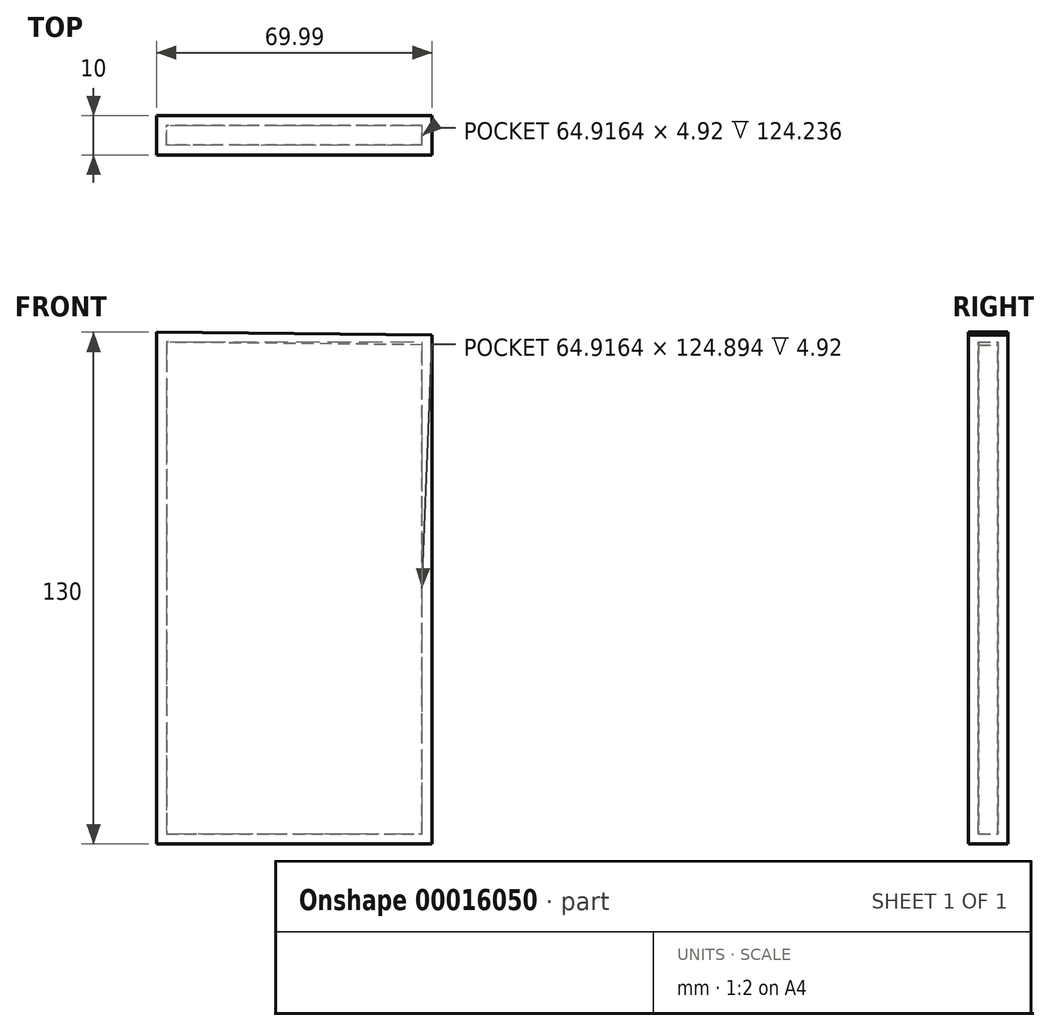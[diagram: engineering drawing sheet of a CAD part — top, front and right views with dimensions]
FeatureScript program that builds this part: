
annotation { "Feature Type Name" : "Feature", "Feature Type Description" : "" }
export const myFeature = defineFeature(function(context is Context, id is Id, definition is map)
    precondition{}
    {
        {
            var Q0;
            Q0=qCreatedBy(makeId("Front.planeOp"),FACE);
            var sketch = newSketch(context, id + "F0", { "sketchPlane" : qUnion([Q0])});
            skLineSegment(sketch, "E0", {"start": v(-56.41, 64.07) * mm, "end": v(-56.41, -65.93) * mm});
            skLineSegment(sketch, "E1", {"start": v(-56.41, -65.93) * mm, "end": v(13.58, -65.93) * mm});
            skLineSegment(sketch, "E2", {"start": v(13.58, -65.93) * mm, "end": v(13.58, 63.36) * mm});
            skLineSegment(sketch, "E3", {"start": v(13.58, 63.36) * mm, "end": v(-56.41, 64.07) * mm});
            skSolve(sketch);
        }
        {
            var Q0;
            Q0 = qSketchRegion(id + "F0", true);
            extrude(context, id + "F1", {"entities" : qUnion([Q0]), "depth" : 10 * mm});
        }
        {
            var Q0;
            Q0=makeQuery(id+"F1.opExtrude","CAP_FACE",FACE,{"disambiguationData":[OSD([sQuery(id+"F0.wireOp",EDGE,"E0"),sQuery(id+"F0.wireOp",EDGE,"E1"),sQuery(id+"F0.wireOp",EDGE,"E2"),sQuery(id+"F0.wireOp",EDGE,"E3")])],"isStart":true});
            var Q1;
            Q1=makeQuery(id+"F1.opExtrude","SWEPT_BODY",BODY,{"disambiguationData":[OSD([sQuery(id+"F0.wireOp",EDGE,"E0"),sQuery(id+"F0.wireOp",EDGE,"E1"),sQuery(id+"F0.wireOp",EDGE,"E2"),sQuery(id+"F0.wireOp",EDGE,"E3")])]});
            shell(context, id + "F2", {"isHollow" : true, "entities" : qUnion([Q0]), "parts" : qUnion([Q1]), "thickness" : 2.54 * mm});
        }
    });
